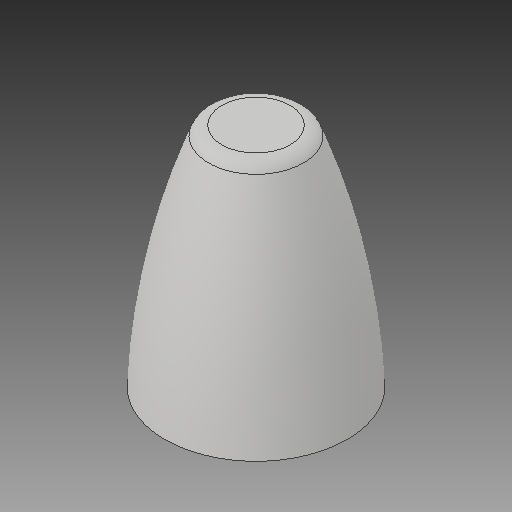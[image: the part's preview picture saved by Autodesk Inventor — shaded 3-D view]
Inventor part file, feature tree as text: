
AUTODESK INVENTOR PART (.ipt)
format: ipt  version: 2018 (Build 220112000, 112)  size: 166,912 bytes
history: native  units: in
note: dims shown in document units (in); Inventor stores cm internally (conversion verified against a paired STEP export)
features: fillet x1
ambient origin geometry x8: Origin, YZ Plane, XZ Plane, XY Plane, X Axis, Y Axis, Z Axis, Center Point
bodies: Solid1 (feature_tree)
feature tree (1):
  fillet  "Fillet3"  [1 undecoded]
note: 1 required parameter value undecoded (feature->parameter linkage not recoverable at this tier; creation-order binding heuristic only, values carry confidence <= 0.55)
